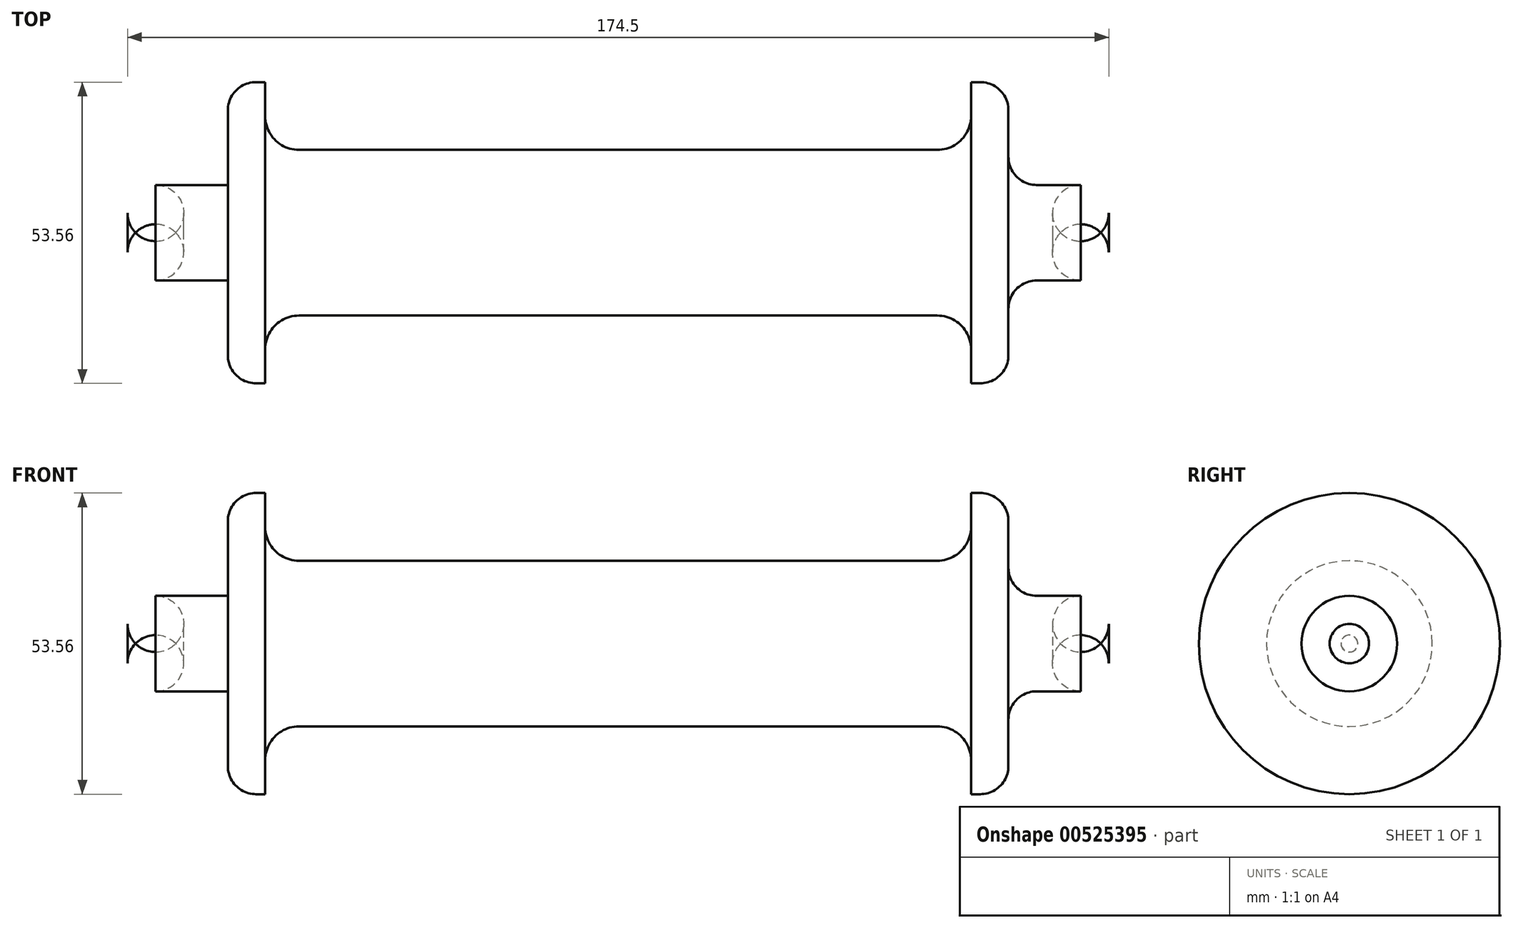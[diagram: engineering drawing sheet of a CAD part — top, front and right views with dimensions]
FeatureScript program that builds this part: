
annotation { "Feature Type Name" : "Feature", "Feature Type Description" : "" }
export const myFeature = defineFeature(function(context is Context, id is Id, definition is map)
    precondition{}
    {
        {
            var Q0;
            Q0=qCreatedBy(makeId("Front.planeOp"),FACE);
            var sketch = newSketch(context, id + "F0", { "sketchPlane" : qUnion([Q0])});
            skLineSegment(sketch, "E0", {"start": v(0, 14.73) * mm, "end": v(56.75, 14.73) * mm});
            skLineSegment(sketch, "E1", {"start": v(62.75, 20.73) * mm, "end": v(62.75, 26.78) * mm});
            skLineSegment(sketch, "E2", {"start": v(62.75, 26.78) * mm, "end": v(69.4, 26.78) * mm});
            skLineSegment(sketch, "E3", {"start": v(69.4, 26.78) * mm, "end": v(69.4, 11.78) * mm});
            skLineSegment(sketch, "E4", {"start": v(69.4, 8.5) * mm, "end": v(87.25, 8.5) * mm});
            skLineSegment(sketch, "E5", {"start": v(87.25, 8.5) * mm, "end": v(87.25, 0) * mm});
            skLineSegment(sketch, "E6", {"start": v(87.25, 0) * mm, "end": v(0, 0) * mm});
            skLineSegment(sketch, "E7", {"start": v(0, 0) * mm, "end": v(0, 14.73) * mm});
            skPoint(sketch, "E8.visualSharp", {"position": v(62.75, 14.73) * mm});
            skArc(sketch, "E8.filletArc", {"start": v(56.75, 14.73) * mm, "mid": v(61, 16.49) * mm, "end": v(62.75, 20.73) * mm});
            skLineSegment(sketch, "E9", {"start": v(69.4, 11.78) * mm, "end": v(69.4, 8.5) * mm});
            skLineSegment(sketch, "E10", {"start": v(-51.52, 0) * mm, "end": v(107.68, 0) * mm, "construction": true});
            skSolve(sketch);
        }
        {
            var Q0;
            Q0 = qSketchRegion(id + "F0", true);
            var Q1;
            Q1=sQuery(id+"F0.wireOp",EDGE,"E6");
            revolve(context, id + "F1", {"entities" : qUnion([Q0]), "axis" : qUnion([Q1]), "revolveType" : RevolveType.FULL});
        }
        {
            var Q0;
            Q0=makeQuery(id+"F1.opRevolve","SWEPT_BODY",BODY,{"disambiguationData":[OSD([sQuery(id+"F0.wireOp",EDGE,"E0"),sQuery(id+"F0.wireOp",EDGE,"E1"),sQuery(id+"F0.wireOp",EDGE,"E2"),sQuery(id+"F0.wireOp",EDGE,"E3"),sQuery(id+"F0.wireOp",EDGE,"E4"),sQuery(id+"F0.wireOp",EDGE,"E5"),sQuery(id+"F0.wireOp",EDGE,"E6"),sQuery(id+"F0.wireOp",EDGE,"E7"),sQuery(id+"F0.wireOp",EDGE,"E8.filletArc"),sQuery(id+"F0.wireOp",EDGE,"E9")])]});
            var Q1;
            Q1=makeQuery(id+"F1.opRevolve","SWEPT_FACE",FACE,{"disambiguationData":[OSD([sQuery(id+"F0.wireOp",EDGE,"E7")])]});
            mirror(context, id + "F2", {"operationType" : NewBodyOperationType.ADD, "entities" : qUnion([Q0]), "mirrorPlane" : qUnion([Q1])});
        }
        {
            var Q0;
            Q0=makeQuery(id+"F2.opPattern","COPY",EDGE,{"derivedFrom":makeQuery(id+"F1.opRevolve","SWEPT_EDGE",EDGE,{"disambiguationData":[OSD([sQuery(id+"F0.wireOp",EDGE,"E4"),sQuery(id+"F0.wireOp",EDGE,"E5")])]}),"instanceName":"1"});
            var Q1;
            Q1=makeQuery(id+"F2.opPattern","COPY",EDGE,{"derivedFrom":makeQuery(id+"F1.opRevolve","SWEPT_EDGE",EDGE,{"disambiguationData":[OSD([sQuery(id+"F0.wireOp",EDGE,"E2"),sQuery(id+"F0.wireOp",EDGE,"E3")])]}),"instanceName":"1"});
            fillet(context, id + "F3", {"entities" : qUnion([Q0, Q1]), "radius" : 5 * mm, "tangentPropagation" : true, "allowEdgeOverflow" : false});
        }
        {
            var Q0;
            Q0=makeQuery(id+"F1.opRevolve","SWEPT_EDGE",EDGE,{"disambiguationData":[OSD([sQuery(id+"F0.wireOp",EDGE,"E2"),sQuery(id+"F0.wireOp",EDGE,"E3")])]});
            var Q1;
            Q1=makeQuery(id+"F1.opRevolve","SWEPT_EDGE",EDGE,{"disambiguationData":[OSD([sQuery(id+"F0.wireOp",EDGE,"E4"),sQuery(id+"F0.wireOp",EDGE,"E9")])]});
            var Q2;
            Q2=makeQuery(id+"F1.opRevolve","SWEPT_EDGE",EDGE,{"disambiguationData":[OSD([sQuery(id+"F0.wireOp",EDGE,"E4"),sQuery(id+"F0.wireOp",EDGE,"E5")])]});
            fillet(context, id + "F4", {"entities" : qUnion([Q0, Q1, Q2]), "radius" : 5 * mm, "tangentPropagation" : true, "allowEdgeOverflow" : false});
        }
    });
